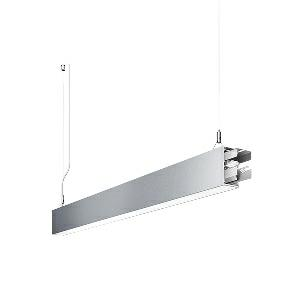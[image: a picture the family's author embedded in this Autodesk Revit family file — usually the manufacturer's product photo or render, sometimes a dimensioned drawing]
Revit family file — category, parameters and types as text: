
# Revit family: dotoo_line_-_dlp_2000_840_d_sta_00805826_c105
name_source: partatom
category: Lighting Fixtures
units: mm (PartAtom-declared; Revit-internal decimal feet)

## family parameters
Cut with Voids When Loaded = No
Host = Face
Light Source = No
Part Type = Normal
Room Calculation Point = No
Round Connector Dimension = Use Diameter
Shared = No

## types (1)
- DOTOO.line - DLP 2000/840/D STA (1 x LED, 1700 lm, 4000K)
    Apparent Load = 16 VA
    Approval mark = CE
    CIE Flux Codes = 67 91 98 100 100
    Color Rendering = 80-89
    Color Temperature = 4000K
    Control Gear = Electronic ballast
    Default Elevation = 1800 mm
    Description = DLP 2000/840/D|Suspended luminaire|light source: LED|connected load: 220-240 V, 50/60 Hz|Power consumption: approx. 16 W|standby: approx. 0,15|luminous flux: 1700 lm|luminous efficacy: 106 lm/W|light distribution: Direct|direct ratio: approx. 100 %|colour temperature: Cold white, ca. 4000 K|color rendering index (CRI): >= 80|chromaticity tolerance:  3 SDCM|System of protection: IP 40|technology: Continuously dimmable|luminaire body|material: Sectional aluminium|colour: Silver|lamp cover: Acrylic (PMMA), Clear|mains lead: 2.00 m With free stranded wires|Fastening: Steel cable 0.3 - 0.7 m|glare control: Prism aperture|luminance(L65): <= 3000 cd/m|unified glare rating(4H 8H): <=  19|special features: DALI Load 1x, TouchDIM - dimming via standard switch, Through-wired, up to 18 m on one mains connection, Flicker-free, Suitable as emergency lighting, Start luminaire with mains connection, Mechanical and electrical connection of the individual modules without tools|
    Frequency = 50 Hz
    Height = 110 mm
    Lamp = 1 x LED
    Lamp Light Flux = 1700 lm
    Lamp count = 1
    Length = 1408 mm
    Luminous efficacy = 106 lm/W
    Manufacturer = Waldmann
    ModVariant = No
    Model = 00805826
    Mounting Place = Ceiling
    Mounting Type = Pendant
    Number of Poles = 1
    OnlyDefault = Yes
    Power Factor = 1
    Product Name = DOTOO.line - DLP 2000/840/D STA
    Product group = Suspended luminaire
    ProductGroupID = 9
    Protection Class = Protection class I
    Protection Degree = IP 40
    RLX_Detail_Level = 1
    RLX_Emergency_Light_Flux = 0 lm
    RLX_Emergency_Type = 0
    RLX_Emergency_Type_DB = No
    RlxData = <blob elided: 23665 chars, md5=17176334>
    Socket = socket
    Standby Power = 0 W
    System Light Flux = 1700 lm
    System Power = 16 W
    Type Comments = Product without accessories
    Type Image = 113310000-00692594.jpg
    URL = http://relux.com
    VarID = ---
    Voltage = 230 V
    Voltage Range = 220-240 V
    Weight = 0.00 kg
    Width = 60 mm  [stored 0.19685 ft]

note: [stored X ft] marks values corroborated as IEEE doubles in the binary element streams (Revit-internal decimal feet)

## geometry (parser evidence)
native form markers: Blend x4, Sweep x12
no freeform markers — native parametric forms only
